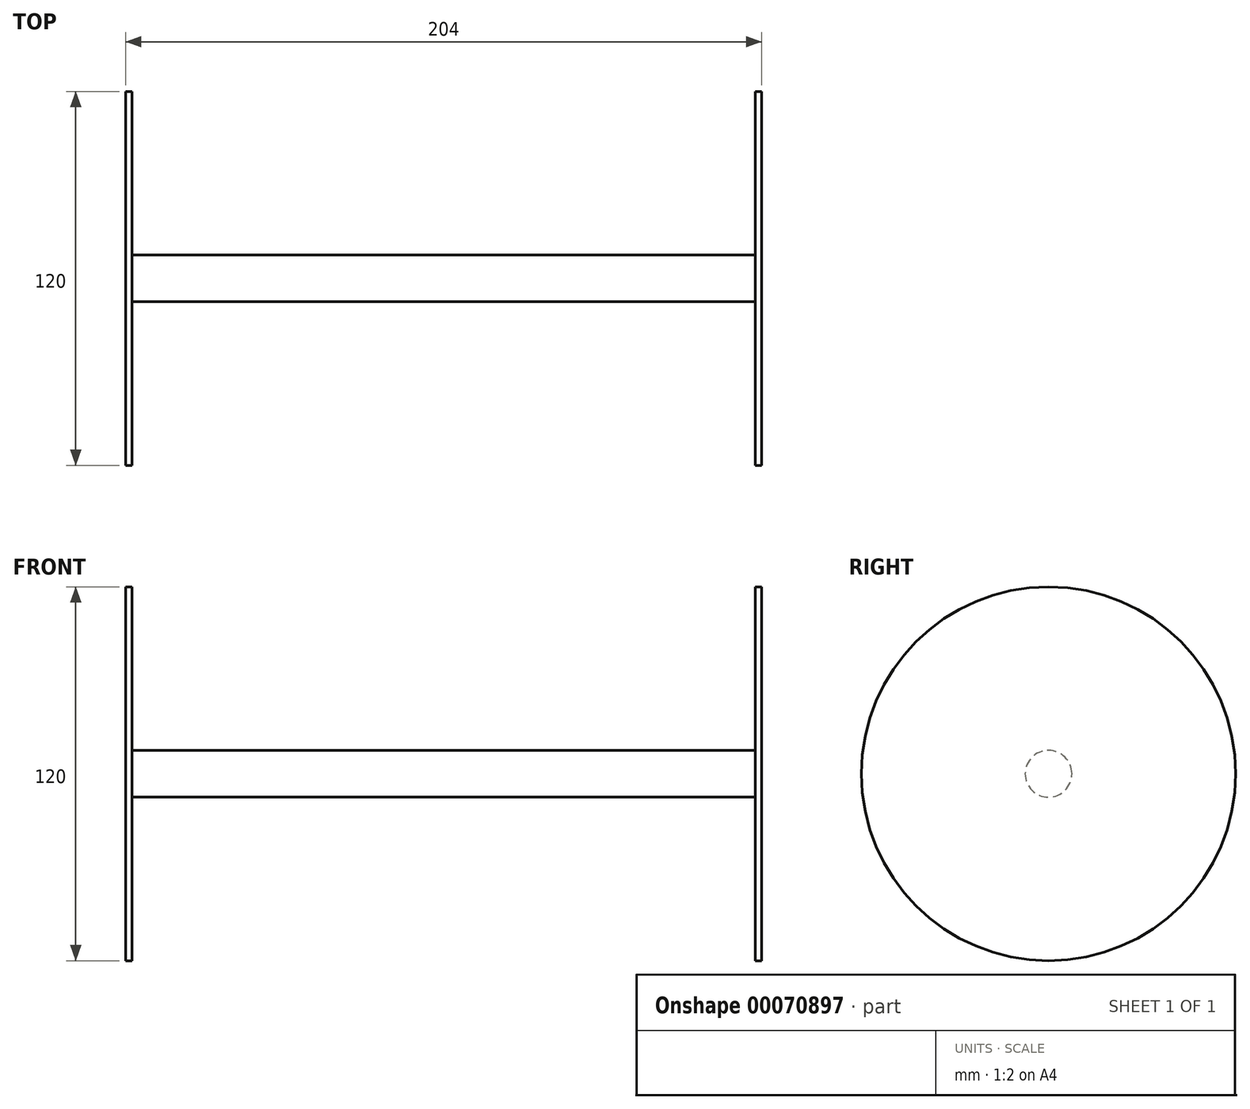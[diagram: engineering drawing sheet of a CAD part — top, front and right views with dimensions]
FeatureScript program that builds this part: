
annotation { "Feature Type Name" : "Feature", "Feature Type Description" : "" }
export const myFeature = defineFeature(function(context is Context, id is Id, definition is map)
    precondition{}
    {
        {
            var Q0;
            Q0=qCreatedBy(makeId("Right.planeOp"),FACE);
            var sketch = newSketch(context, id + "F0", { "sketchPlane" : qUnion([Q0])});
            skCircle(sketch, "E0", {"center": v(0, 0) * mm, "radius": 60 * mm});
            skCircle(sketch, "E1", {"center": v(0, 0) * mm, "radius": 7.5 * mm});
            skSolve(sketch);
        }
        {
            var Q0;
            Q0=makeQuery(id+"F0.imprint","IMPRINT",FACE,{"disambiguationData":[TD([[makeQuery(id+"F0.imprint","IMPRINT",EDGE,{"derivedFrom":sQuery(id+"F0.wireOp",EDGE,"E1")}),1.0]])]});
            var Q1;
            Q1=makeQuery(id+"F0.imprint","IMPRINT",FACE,{"disambiguationData":[TD([[makeQuery(id+"F0.imprint","IMPRINT",EDGE,{"derivedFrom":sQuery(id+"F0.wireOp",EDGE,"E0")}),1.0]])]});
            extrude(context, id + "F1", {"entities" : qUnion([Q0, Q1]), "depth" : 2 * mm});
        }
        {
            var Q0;
            Q0=makeQuery(id+"F1.opExtrude","CAP_FACE",FACE,{"disambiguationData":[OSD([sQuery(id+"F0.wireOp",EDGE,"E0")])],"isStart":false});
            var sketch = newSketch(context, id + "F2", { "sketchPlane" : qUnion([Q0])});
            skCircle(sketch, "E2", {"center": v(0, 0) * mm, "radius": 7.5 * mm});
            skSolve(sketch);
        }
        {
            var Q0;
            Q0 = qSketchRegion(id + "F2", true);
            extrude(context, id + "F3", {"entities" : qUnion([Q0]), "operationType" : NewBodyOperationType.ADD, "depth" : 200 * mm});
        }
        {
            var Q0;
            Q0=makeQuery(id+"F3.opExtrude","CAP_FACE",FACE,{"disambiguationData":[OSD([sQuery(id+"F2.wireOp",EDGE,"E2")])],"isStart":false});
            var sketch = newSketch(context, id + "F4", { "sketchPlane" : qUnion([Q0])});
            skSolve(sketch);
        }
        {
            var Q0;
            Q0=makeQuery(id+"F4.imprint","IMPRINT",FACE,{"disambiguationData":[TD([[makeQuery(id+"F4.imprint","IMPRINT",EDGE,{"derivedFrom":makeQuery(id+"F3.opExtrude","CAP_EDGE",EDGE,{"disambiguationData":[OSD([sQuery(id+"F2.wireOp",EDGE,"E2")])],"isStart":false})}),1.0]])]});
            var sketch = newSketch(context, id + "F5", { "sketchPlane" : qUnion([Q0])});
            skCircle(sketch, "E3", {"center": v(0, 0) * mm, "radius": 60 * mm});
            skSolve(sketch);
        }
        {
            var Q0;
            Q0 = qSketchRegion(id + "F5", true);
            extrude(context, id + "F6", {"entities" : qUnion([Q0]), "operationType" : NewBodyOperationType.ADD, "depth" : 2 * mm});
        }
    });
